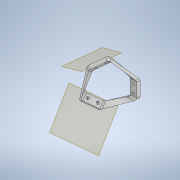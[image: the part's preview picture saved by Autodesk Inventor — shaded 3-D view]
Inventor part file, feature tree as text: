
AUTODESK INVENTOR PART (.ipt)
format: ipt  version: 2020 (Build 240168000, 168)  size: 510,976 bytes
history: native  units: mm
features: other x11, extrude x3, loft x3, fillet x3, sketch x3, reference x3, plane x2
ambient origin geometry x8: Origin, YZ Plane, XZ Plane, XY Plane, X Axis, Y Axis, Z Axis, Center Point
bodies: Solid1 (feature_tree)
feature tree (28):
  extrude  "Extrusion1"  Depth=3.0mm
  plane  "Work Plane1"
  extrude  "Extrusion2"  Depth=3.0mm
  plane  "Work Plane2"
  extrude  "Extrusion3"  Depth=4.0mm TaperAngle=0.0deg
  loft  "Loft1"
  loft  "Loft2"
  loft  "Loft3"
  fillet  "Fillet1"  [1 undecoded]
  fillet  "Fillet2"  [1 undecoded]
  fillet  "Fillet3"  [1 undecoded]
  sketch  "Sketch1"  dims[d0=3.0mm d1=3.0mm]
  reference  "Reference1"
  sketch  "Sketch2"  dims[d2=4.0mm d3=0.0mm d4=3.0mm]
  reference  "Reference2"
  sketch  "Sketch3"  dims[d5=3.0mm d6=4.0mm d7=0.0mm d8=3.0mm d9=3.0mm d10=4.0mm d11=0.0mm d12=0.0mm d13=90.0deg d14=0.0mm d15=90.0deg d16=0.0mm d17=90.0deg d18=0.0mm d19=90.0deg d20=0.0mm d21=90.0deg d22=0.0mm d23=90.0deg d24=3.0mm d25=3.0mm d26=3.0mm]
  reference  "Reference3"
  other  "Edges1"
  other  "Edges2"
  other  "Edges3"
  other  "Edges4"
  other  "Edges5"
  other  "Edges6"
  parser-record x1  (decoder bookkeeping rows leaked as tree rows — omitted from the tree; the rows remain in map.json)
  other  "delta_1.iam"
  other  "arm_holder_2:2"
  other  "arm_holder_2:3"
  other  "arm_holder_2:1"
note: 3 required parameter values undecoded (feature->parameter linkage not recoverable at this tier; creation-order binding heuristic only, values carry confidence <= 0.55)
note: 1 file-system path scrubbed to <path> (originals preserved in map.json)
